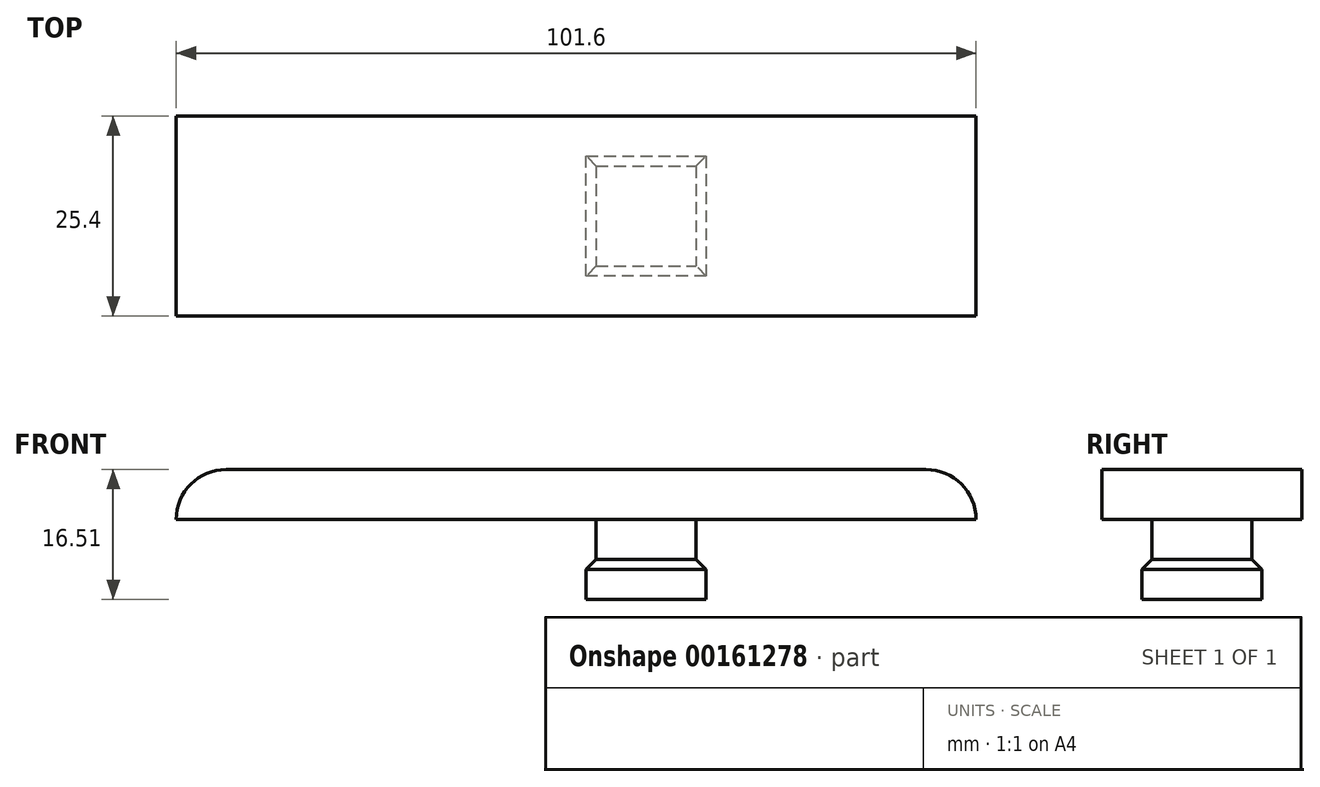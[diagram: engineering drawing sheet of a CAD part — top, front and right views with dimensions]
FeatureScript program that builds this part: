
annotation { "Feature Type Name" : "Feature", "Feature Type Description" : "" }
export const myFeature = defineFeature(function(context is Context, id is Id, definition is map)
    precondition{}
    {
        {
            var Q0;
            Q0=qCreatedBy(makeId("Top.planeOp"),FACE);
            var sketch = newSketch(context, id + "F0", { "sketchPlane" : qUnion([Q0])});
            skLineSegment(sketch, "E0.bottom", {"start": v(50.8, 12.7) * mm, "end": v(-50.8, 12.7) * mm});
            skLineSegment(sketch, "E0.top", {"start": v(50.8, -12.7) * mm, "end": v(-50.8, -12.7) * mm});
            skLineSegment(sketch, "E0.left", {"start": v(50.8, 12.7) * mm, "end": v(50.8, -12.7) * mm});
            skLineSegment(sketch, "E0.right", {"start": v(-50.8, 12.7) * mm, "end": v(-50.8, -12.7) * mm});
            skPoint(sketch, "E0.middle", {"position": v(0, 0) * mm});
            skLineSegment(sketch, "E1.bottom", {"start": v(2.54, 6.35) * mm, "end": v(15.24, 6.35) * mm});
            skLineSegment(sketch, "E1.top", {"start": v(2.54, -6.35) * mm, "end": v(15.24, -6.35) * mm});
            skLineSegment(sketch, "E1.left", {"start": v(2.54, 6.35) * mm, "end": v(2.54, -6.35) * mm});
            skLineSegment(sketch, "E1.right", {"start": v(15.24, 6.35) * mm, "end": v(15.24, -6.35) * mm});
            skSolve(sketch);
        }
        {
            var Q0;
            Q0=makeQuery(id+"F0.imprint","IMPRINT",FACE,{"disambiguationData":[TD([[makeQuery(id+"F0.imprint","IMPRINT",EDGE,{"derivedFrom":sQuery(id+"F0.wireOp",EDGE,"E0.bottom")}),1.0]])]});
            var Q1;
            Q1=makeQuery(id+"F0.imprint","IMPRINT",FACE,{"disambiguationData":[TD([[makeQuery(id+"F0.imprint","IMPRINT",EDGE,{"derivedFrom":sQuery(id+"F0.wireOp",EDGE,"E1.bottom")}),-1.0]])]});
            extrude(context, id + "F1", {"entities" : qUnion([Q0, Q1]), "depth" : 6.35 * mm});
        }
        {
            var Q0;
            Q0=makeQuery(id+"F1.opExtrude","CAP_EDGE",EDGE,{"disambiguationData":[OSD([sQuery(id+"F0.wireOp",EDGE,"E0.right")])],"isStart":false});
            fillet(context, id + "F2", {"entities" : qUnion([Q0]), "radius" : 6.35 * mm, "tangentPropagation" : true, "allowEdgeOverflow" : false});
        }
        {
            var Q0;
            Q0=makeQuery(id+"F1.opExtrude","CAP_EDGE",EDGE,{"disambiguationData":[OSD([sQuery(id+"F0.wireOp",EDGE,"E0.left")])],"isStart":false});
            fillet(context, id + "F3", {"entities" : qUnion([Q0]), "radius" : 6.35 * mm, "tangentPropagation" : true, "allowEdgeOverflow" : false});
        }
        {
            var Q0;
            Q0=makeQuery(id+"F0.imprint","IMPRINT",FACE,{"disambiguationData":[TD([[makeQuery(id+"F0.imprint","IMPRINT",EDGE,{"derivedFrom":sQuery(id+"F0.wireOp",EDGE,"E1.bottom")}),-1.0]])]});
            extrude(context, id + "F4", {"entities" : qUnion([Q0]), "operationType" : NewBodyOperationType.ADD, "oppositeDirection" : true, "depth" : 3.8 * mm});
        }
        {
            var Q0;
            Q0=makeQuery(id+"F4.opExtrude","CAP_FACE",FACE,{"disambiguationData":[OSD([sQuery(id+"F0.wireOp",EDGE,"E1.bottom"),sQuery(id+"F0.wireOp",EDGE,"E1.top"),sQuery(id+"F0.wireOp",EDGE,"E1.left"),sQuery(id+"F0.wireOp",EDGE,"E1.right")])],"isStart":false});
            var sketch = newSketch(context, id + "F5", { "sketchPlane" : qUnion([Q0])});
            skLineSegment(sketch, "E2.bottom", {"start": v(16.5, 7.62) * mm, "end": v(1.27, 7.62) * mm});
            skLineSegment(sketch, "E2.top", {"start": v(16.5, -7.62) * mm, "end": v(1.27, -7.62) * mm});
            skLineSegment(sketch, "E2.left", {"start": v(16.5, 7.62) * mm, "end": v(16.5, -7.62) * mm});
            skLineSegment(sketch, "E2.right", {"start": v(1.27, 7.62) * mm, "end": v(1.27, -7.62) * mm});
            skPoint(sketch, "E2.middle", {"position": v(8.89, 0) * mm});
            skPoint(sketch, "E2.middle.positionSnap0", {"position": v(15.24, 0) * mm});
            skPoint(sketch, "E2.middle.positionSnap1", {"position": v(8.89, 6.35) * mm});
            skPoint(sketch, "E2.centerSnap0", {"position": v(15.24, 0) * mm});
            skPoint(sketch, "E2.centerSnap1", {"position": v(8.89, 6.35) * mm});
            skSolve(sketch);
        }
        {
            var Q0;
            Q0=makeQuery(id+"F5.imprint","IMPRINT",FACE,{"disambiguationData":[TD([[makeQuery(id+"F5.imprint","IMPRINT",EDGE,{"derivedFrom":sQuery(id+"F5.wireOp",EDGE,"E2.bottom")}),1.0]])]});
            var Q1;
            Q1=makeQuery(id+"F5.imprint","IMPRINT",FACE,{"disambiguationData":[TD([[makeQuery(id+"F5.imprint","IMPRINT",EDGE,{"derivedFrom":makeQuery(id+"F4.opExtrude","CAP_EDGE",EDGE,{"disambiguationData":[OSD([sQuery(id+"F0.wireOp",EDGE,"E1.bottom")])],"isStart":false})}),1.0]])]});
            extrude(context, id + "F6", {"entities" : qUnion([Q0, Q1]), "operationType" : NewBodyOperationType.ADD, "depth" : 6.35 * mm});
        }
        {
            var Q0;
            Q0=makeQuery(id+"F6.opExtrude","CAP_EDGE",EDGE,{"disambiguationData":[OSD([sQuery(id+"F5.wireOp",EDGE,"E2.right")])],"isStart":true});
            var Q1;
            Q1=makeQuery(id+"F6.opExtrude","CAP_EDGE",EDGE,{"disambiguationData":[OSD([sQuery(id+"F5.wireOp",EDGE,"E2.bottom")])],"isStart":true});
            var Q2;
            Q2=makeQuery(id+"F6.opExtrude","CAP_EDGE",EDGE,{"disambiguationData":[OSD([sQuery(id+"F5.wireOp",EDGE,"E2.left")])],"isStart":true});
            var Q3;
            Q3=makeQuery(id+"F6.opExtrude","CAP_EDGE",EDGE,{"disambiguationData":[OSD([sQuery(id+"F5.wireOp",EDGE,"E2.top")])],"isStart":true});
            chamfer(context, id + "F7", {"entities" : qUnion([Q0, Q1, Q2, Q3]), "width" : 2.54 * mm, "tangentPropagation" : true});
        }
    });
